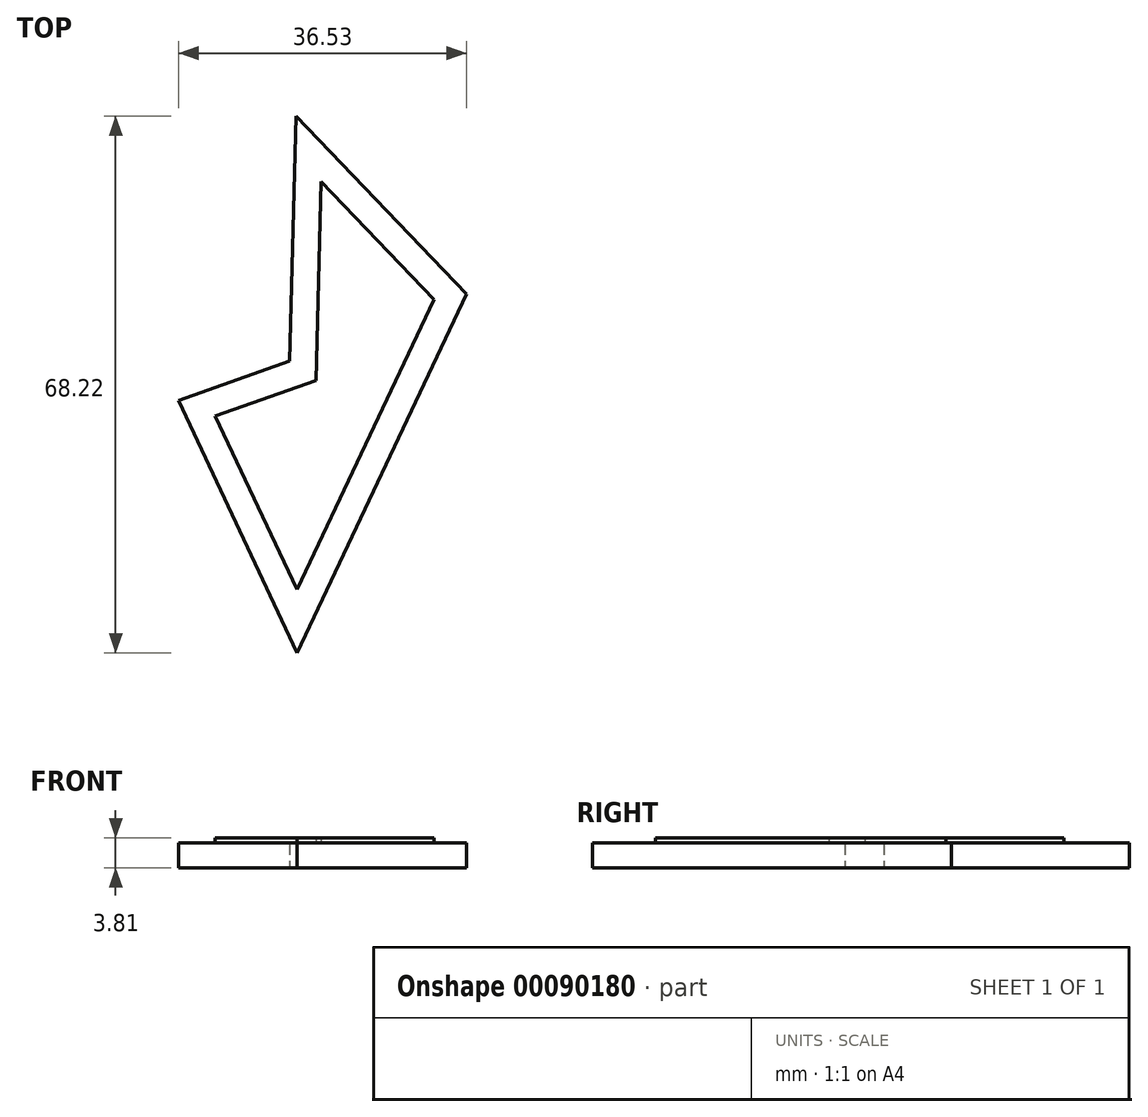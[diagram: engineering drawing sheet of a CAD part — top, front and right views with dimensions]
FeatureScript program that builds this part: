
annotation { "Feature Type Name" : "Feature", "Feature Type Description" : "" }
export const myFeature = defineFeature(function(context is Context, id is Id, definition is map)
    precondition{}
    {
        {
            var Q0;
            Q0=qCreatedBy(makeId("Top.planeOp"),FACE);
            var sketch = newSketch(context, id + "F0", { "sketchPlane" : qUnion([Q0])});
            skLineSegment(sketch, "E0", {"start": v(32.45, 33.52) * mm, "end": v(31.68, 2.36) * mm});
            skLineSegment(sketch, "E1", {"start": v(31.68, 2.37) * mm, "end": v(17.59, -2.62) * mm});
            skLineSegment(sketch, "E2", {"start": v(17.47, -2.65) * mm, "end": v(32.62, -34.75) * mm});
            skLineSegment(sketch, "E3", {"start": v(32.57, -34.75) * mm, "end": v(54.12, 10.88) * mm});
            skLineSegment(sketch, "E4", {"start": v(54.15, 10.89) * mm, "end": v(32.47, 33.54) * mm});
            skFitSpline(sketch, "E5", {"points": [v(-23.76, -1.65) * mm, v(-23.76, -1.65) * mm, v(9.9, -13.7) * mm, v(9.73, -13.7) * mm, v(-23.76, -1.65) * mm]});
            skFitSpline(sketch, "E6", {"points": [v(9.73, -13.7) * mm, v(9.55, -13.7) * mm, v(-7.36, 33.88) * mm, v(-7.36, 33.88) * mm, v(9.73, -13.7) * mm]});
            skLineSegment(sketch, "E7", {"start": v(32.45, 33.52) * mm, "end": v(54.12, 10.88) * mm});
            skLineSegment(sketch, "E8", {"start": v(32.62, -34.75) * mm, "end": v(17.59, -2.62) * mm});
            skLineSegment(sketch, "E9", {"start": v(31.68, 2.36) * mm, "end": v(32.45, 33.52) * mm});
            skLineSegment(sketch, "E10.0", {"start": v(32.6, -26.66) * mm, "end": v(50.01, 10.22) * mm});
            skLineSegment(sketch, "E10.1", {"start": v(35.68, 25.2) * mm, "end": v(50.01, 10.22) * mm});
            skLineSegment(sketch, "E10.2", {"start": v(22.2, -4.63) * mm, "end": v(32.6, -26.66) * mm});
            skLineSegment(sketch, "E10.3", {"start": v(35.05, -0.08) * mm, "end": v(22.2, -4.63) * mm});
            skLineSegment(sketch, "E10.4", {"start": v(35.05, -0.08) * mm, "end": v(35.68, 25.2) * mm});
            skSolve(sketch);
        }
        {
            var Q0;
            Q0=makeQuery(id+"F0.imprint","IMPRINT",FACE,{"disambiguationData":[TD([[makeQuery(id+"F0.imprint","IMPRINT",EDGE,{"derivedFrom":sQuery(id+"F0.wireOp",EDGE,"E10.0")}),1.0]])]});
            extrude(context, id + "F1", {"entities" : qUnion([Q0]), "depth" : 3.8 * mm});
        }
        {
            var Q0;
            {var subQ5=sQuery(id+"F0.wireOp",EDGE,"E7");Q0=makeQuery(id+"F0.imprint","IMPRINT",FACE,{"disambiguationData":[TD([[makeQuery(id+"F0.imprint","IMPRINT",EDGE,{"derivedFrom":subQ5}),-1.0]])]});}
            extrude(context, id + "F2", {"entities" : qUnion([Q0]), "operationType" : NewBodyOperationType.ADD, "depth" : 3.17 * mm});
        }
    });
